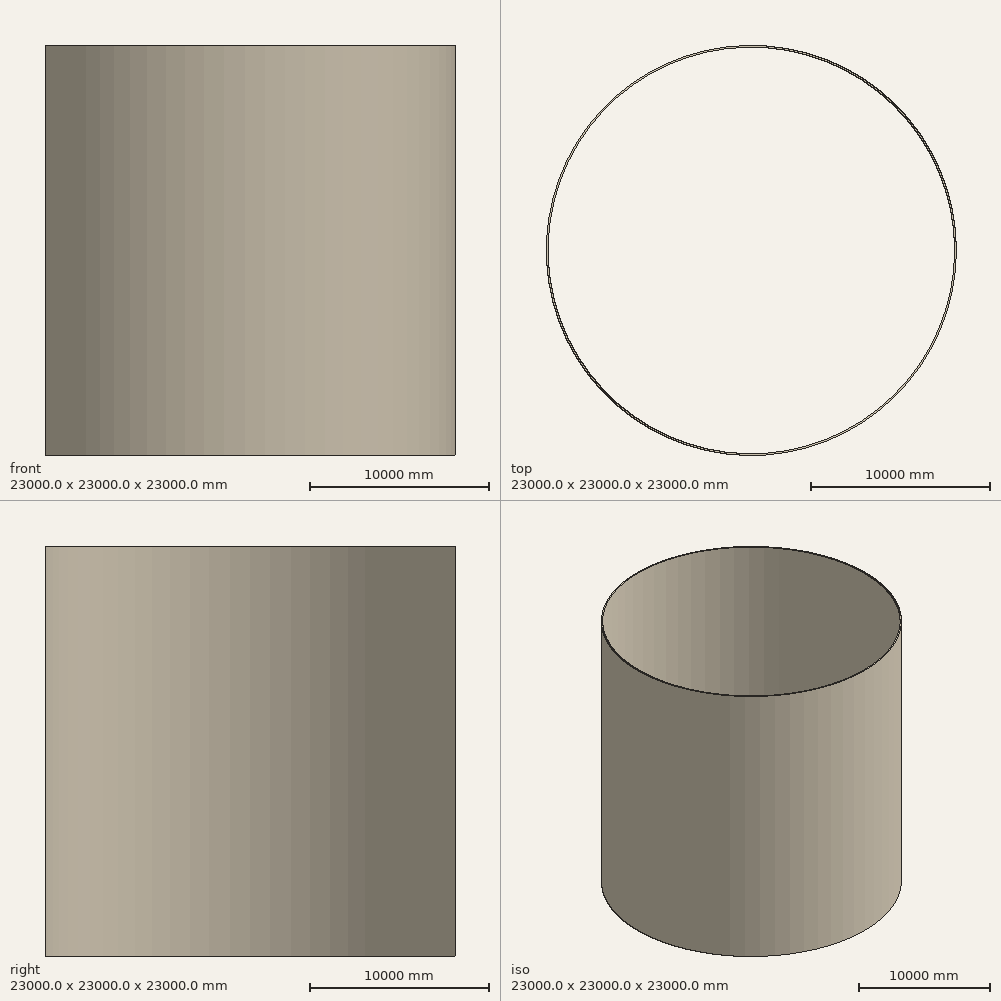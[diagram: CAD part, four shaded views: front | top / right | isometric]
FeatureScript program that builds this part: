
annotation { "Feature Type Name" : "Feature", "Feature Type Description" : "" }
export const myFeature = defineFeature(function(context is Context, id is Id, definition is map)
    precondition{}
    {
        {
            var Q0;
            Q0=qCreatedBy(makeId("Top.planeOp"),FACE);
            var sketch = newSketch(context, id + "F0", { "sketchPlane" : qUnion([Q0])});
            skCircle(sketch, "E0", {"center": v(0, 0) * mm, "radius": 11500 * mm});
            skCircle(sketch, "E1", {"center": v(0, 0) * mm, "radius": 11400 * mm});
            skSolve(sketch);
        }
        {
            var Q0;
            Q0=makeQuery(id+"F0.imprint","IMPRINT",FACE,{"disambiguationData":[TD([[makeQuery(id+"F0.imprint","IMPRINT",EDGE,{"derivedFrom":sQuery(id+"F0.wireOp",EDGE,"E0")}),1.0]])]});
            extrude(context, id + "F1", {"entities" : qUnion([Q0]), "depth" : 23000 * mm, "offsetDistance" : 25.4 * mm});
        }
    });
